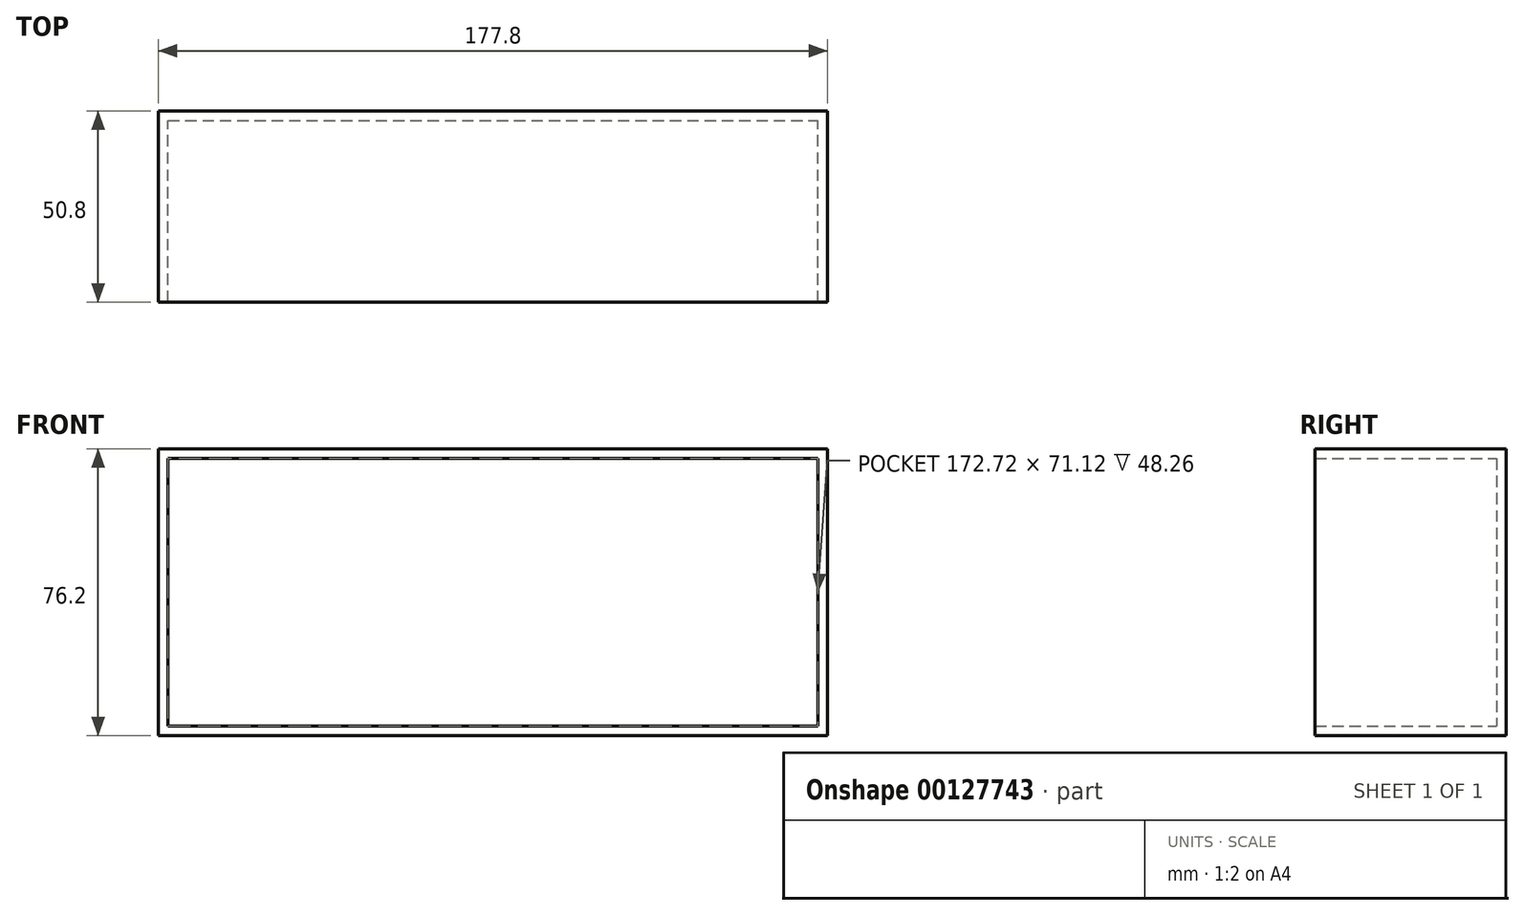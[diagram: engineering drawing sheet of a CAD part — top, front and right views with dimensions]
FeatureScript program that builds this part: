
annotation { "Feature Type Name" : "Feature", "Feature Type Description" : "" }
export const myFeature = defineFeature(function(context is Context, id is Id, definition is map)
    precondition{}
    {
        {
            var Q0;
            Q0=qCreatedBy(makeId("Front.planeOp"),FACE);
            var sketch = newSketch(context, id + "F0", { "sketchPlane" : qUnion([Q0])});
            skLineSegment(sketch, "E0.bottom", {"start": v(-88.9, 38.1) * mm, "end": v(88.9, 38.1) * mm});
            skLineSegment(sketch, "E0.top", {"start": v(-88.9, -38.1) * mm, "end": v(88.9, -38.1) * mm});
            skLineSegment(sketch, "E0.left", {"start": v(-88.9, 38.1) * mm, "end": v(-88.9, -38.1) * mm});
            skLineSegment(sketch, "E0.right", {"start": v(88.9, 38.1) * mm, "end": v(88.9, -38.1) * mm});
            skPoint(sketch, "E0.middle", {"position": v(0, 0) * mm});
            skSolve(sketch);
        }
        {
            var Q0;
            Q0=makeQuery(id+"F0.imprint","IMPRINT",FACE,{"disambiguationData":[TD([[makeQuery(id+"F0.imprint","IMPRINT",EDGE,{"derivedFrom":sQuery(id+"F0.wireOp",EDGE,"E0.bottom")}),-1.0]])]});
            extrude(context, id + "F1", {"entities" : qUnion([Q0]), "depth" : 50.8 * mm});
        }
        {
            var Q0;
            Q0=makeQuery(id+"F1.opExtrude","CAP_FACE",FACE,{"disambiguationData":[OSD([sQuery(id+"F0.wireOp",EDGE,"E0.bottom"),sQuery(id+"F0.wireOp",EDGE,"E0.top"),sQuery(id+"F0.wireOp",EDGE,"E0.left"),sQuery(id+"F0.wireOp",EDGE,"E0.right")])],"isStart":false});
            var sketch = newSketch(context, id + "F2", { "sketchPlane" : qUnion([Q0])});
            skCircle(sketch, "E1", {"center": v(0, 0) * mm, "radius": 25.4 * mm});
            skSolve(sketch);
        }
        {
            var Q0;
            Q0=makeQuery(id+"F1.opExtrude","CAP_FACE",FACE,{"disambiguationData":[OSD([sQuery(id+"F0.wireOp",EDGE,"E0.bottom"),sQuery(id+"F0.wireOp",EDGE,"E0.top"),sQuery(id+"F0.wireOp",EDGE,"E0.left"),sQuery(id+"F0.wireOp",EDGE,"E0.right")])],"isStart":false});
            shell(context, id + "F3", {"entities" : qUnion([Q0]), "thickness" : 2.54 * mm});
        }
        {
            var Q0;
            Q0=sQuery(id+"F2.wireOp",EDGE,"E1");
            extrude(context, id + "F4", {"bodyType" : ToolBodyType.SURFACE, "surfaceEntities" : qUnion([Q0]), "oppositeDirection" : true, "depth" : 2.54 * mm});
        }
    });
